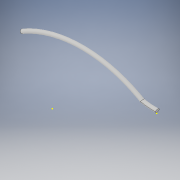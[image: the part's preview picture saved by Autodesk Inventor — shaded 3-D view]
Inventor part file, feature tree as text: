
AUTODESK INVENTOR PART (.ipt)
format: ipt  version: 2017 (Build 210142000, 142)  size: 134,144 bytes
history: native  units: in
note: dims shown in document units (in); Inventor stores cm internally (conversion verified against a paired STEP export)
features: sketch x11, plane x3, sweep x2
ambient origin geometry x8: Origin, YZ Plane, XZ Plane, XY Plane, X Axis, Y Axis, Z Axis, Center Point
bodies: Solid1 (feature_tree)
feature tree (16):
  sketch  "Sketch1"  dims[d0=8.0in d1=8.0in]
  plane  "Work Plane1"
  plane  "Work Plane2"
  sketch  "Sketch2"  dims[d2=0.25in d3=0.25in]
  sweep  "Sweep1"
  sketch  "Sketch4"  dims[d6=1.0in]
  sketch  "Sketch5"  dims[d7=0.0in d8=0.0in]
  sketch  "Sketch6"
  sketch  "Sketch7"
  plane  "Work Plane3"
  sweep  "Sweep2"
  sketch  "Sketch10"
  sketch  "Sketch11"
  sketch  "Sketch3"  dims[d4=0.0in d5=0.0in]
  sketch  "Sketch8"
  sketch  "Sketch9"
